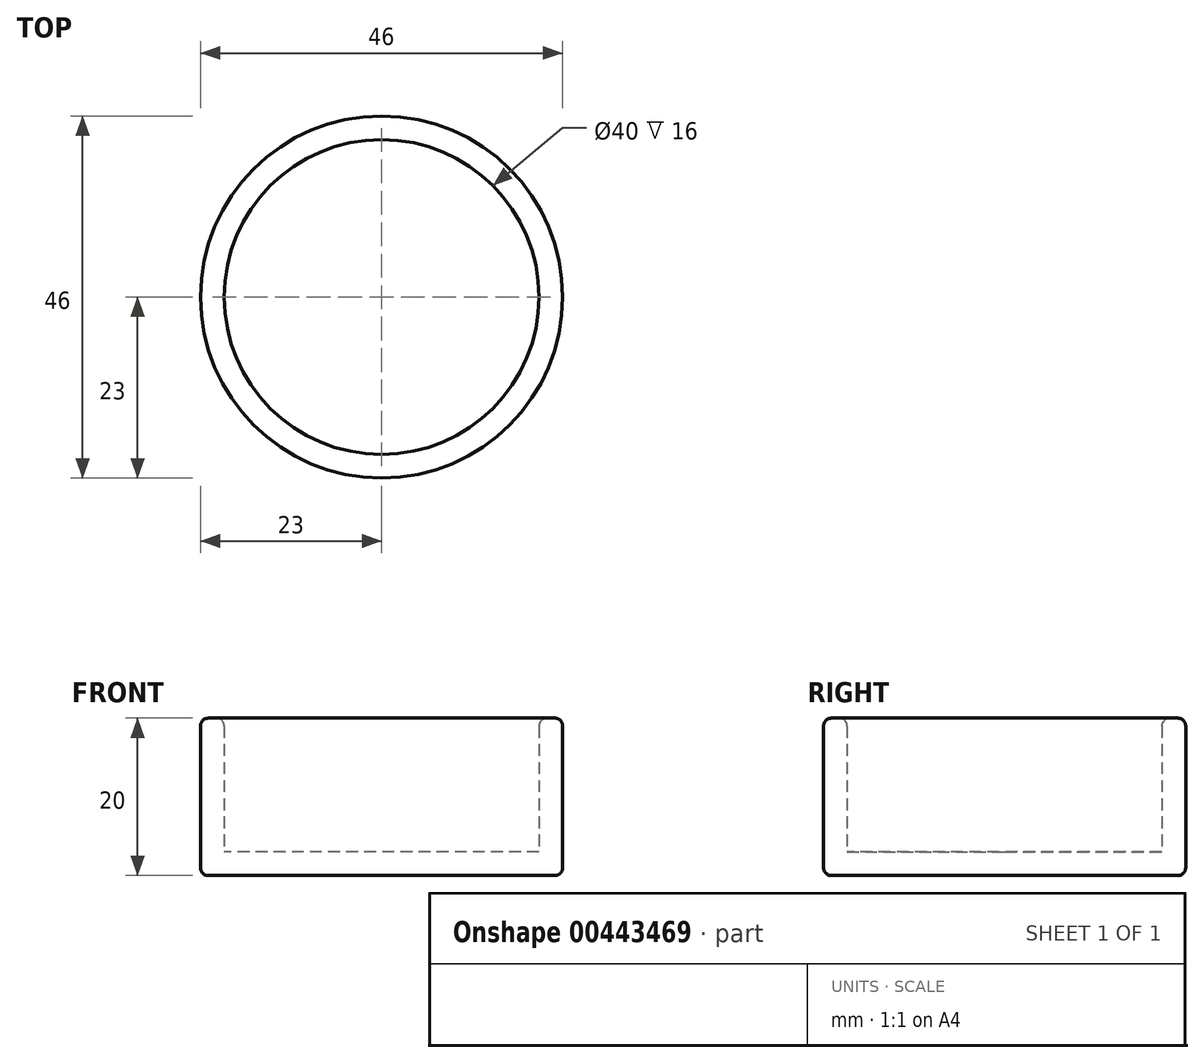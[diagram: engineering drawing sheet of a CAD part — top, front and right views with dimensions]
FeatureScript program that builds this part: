
annotation { "Feature Type Name" : "Feature", "Feature Type Description" : "" }
export const myFeature = defineFeature(function(context is Context, id is Id, definition is map)
    precondition{}
    {
        {
            var Q0;
            Q0=qCreatedBy(makeId("Top.planeOp"),FACE);
            var sketch = newSketch(context, id + "F0", { "sketchPlane" : qUnion([Q0])});
            skCircle(sketch, "E0", {"center": v(0, 0) * mm, "radius": 23 * mm});
            skCircle(sketch, "E1", {"center": v(0, 0) * mm, "radius": 20 * mm});
            skSolve(sketch);
        }
        {
            var Q0;
            Q0 = qSketchRegion(id + "F0", true);
            extrude(context, id + "F1", {"entities" : qUnion([Q0]), "depth" : 20 * mm});
        }
        {
            var Q0;
            Q0=qCreatedBy(makeId("Top.planeOp"),FACE);
            var sketch = newSketch(context, id + "F2", { "sketchPlane" : qUnion([Q0])});
            skCircle(sketch, "E2", {"center": v(0, 0) * mm, "radius": 23 * mm});
            skSolve(sketch);
        }
        {
            var Q0;
            Q0 = qSketchRegion(id + "F2", true);
            extrude(context, id + "F3", {"entities" : qUnion([Q0]), "operationType" : NewBodyOperationType.ADD, "depth" : 3 * mm});
        }
        {
            var Q0;
            Q0=makeQuery(id+"F1.opExtrude","CAP_EDGE",EDGE,{"disambiguationData":[OSD([sQuery(id+"F0.wireOp",EDGE,"E1")])],"isStart":false});
            var Q1;
            Q1=makeQuery(id+"F1.opExtrude","CAP_EDGE",EDGE,{"disambiguationData":[OSD([sQuery(id+"F0.wireOp",EDGE,"E0")])],"isStart":false});
            var Q2;
            Q2=makeQuery(id+"F1.opExtrude","CAP_EDGE",EDGE,{"disambiguationData":[OSD([sQuery(id+"F0.wireOp",EDGE,"E0")])],"isStart":true});
            fillet(context, id + "F4", {"entities" : qUnion([Q0, Q1, Q2]), "radius" : 1 * mm, "tangentPropagation" : true, "allowEdgeOverflow" : false});
        }
    });
